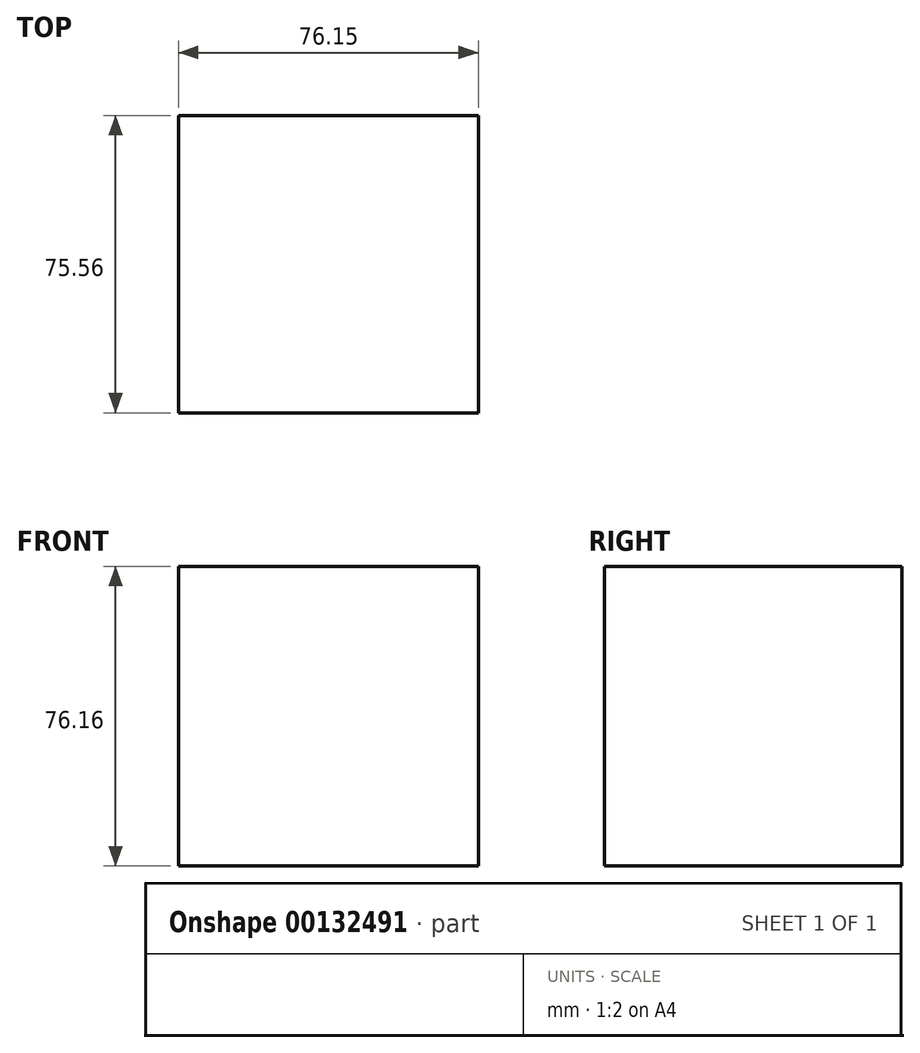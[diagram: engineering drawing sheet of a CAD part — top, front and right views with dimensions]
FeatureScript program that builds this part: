
annotation { "Feature Type Name" : "Feature", "Feature Type Description" : "" }
export const myFeature = defineFeature(function(context is Context, id is Id, definition is map)
    precondition{}
    {
        {
            var Q0;
            Q0=qCreatedBy(makeId("Front.planeOp"),FACE);
            var sketch = newSketch(context, id + "F0", { "sketchPlane" : qUnion([Q0])});
            skLineSegment(sketch, "E0", {"start": v(0, 0) * mm, "end": v(76.15, 0) * mm});
            skLineSegment(sketch, "E1", {"start": v(76.15, 0) * mm, "end": v(76.15, 76.16) * mm});
            skLineSegment(sketch, "E2", {"start": v(76.15, 76.16) * mm, "end": v(0, 76.16) * mm});
            skLineSegment(sketch, "E3", {"start": v(0, 76.16) * mm, "end": v(0, 0) * mm});
            skSolve(sketch);
        }
        {
            var Q0;
            Q0=makeQuery(id+"F0.imprint","IMPRINT",FACE,{"disambiguationData":[TD([[makeQuery(id+"F0.imprint","IMPRINT",EDGE,{"derivedFrom":sQuery(id+"F0.wireOp",EDGE,"E0")}),1.0]])]});
            extrude(context, id + "F1", {"entities" : qUnion([Q0]), "depth" : 75.56 * mm});
        }
    });
